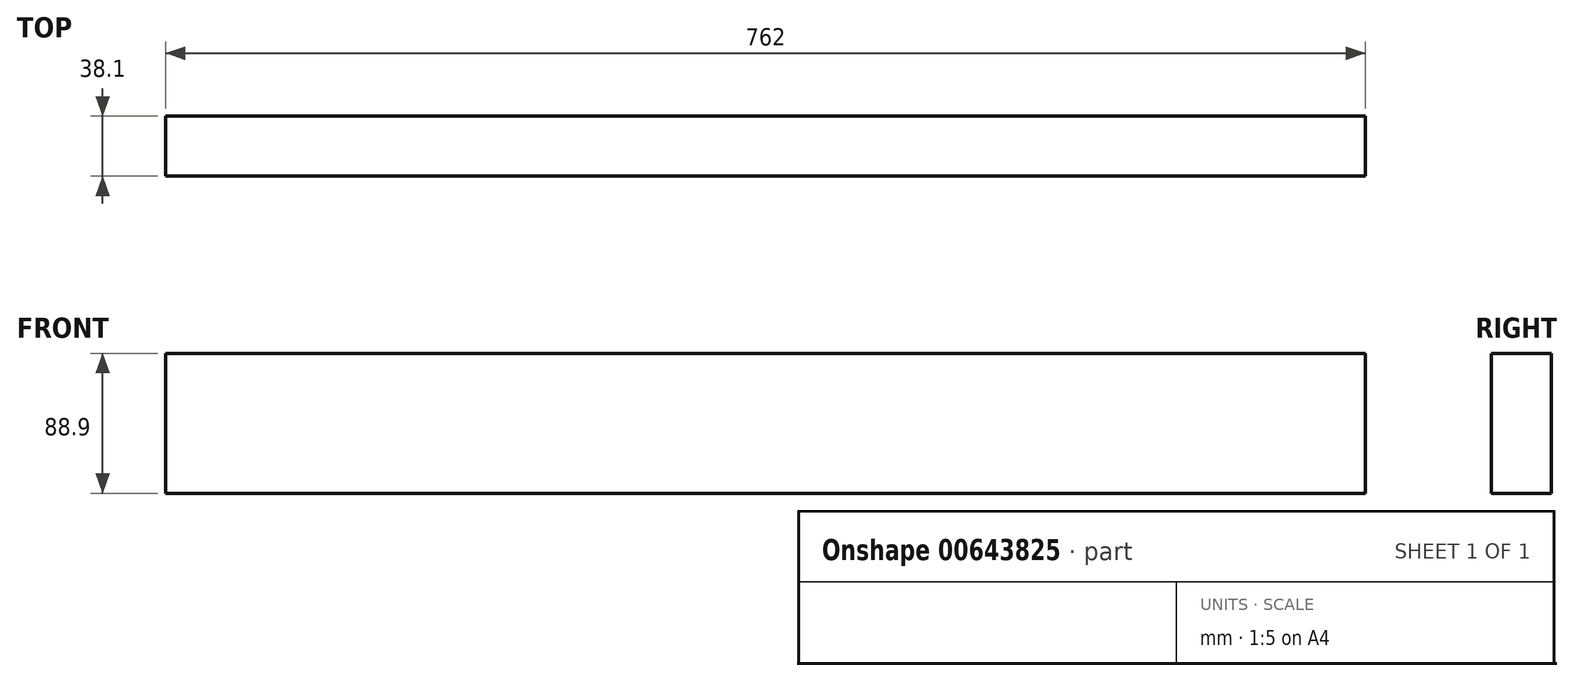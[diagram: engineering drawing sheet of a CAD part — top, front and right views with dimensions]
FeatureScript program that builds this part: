
annotation { "Feature Type Name" : "Feature", "Feature Type Description" : "" }
export const myFeature = defineFeature(function(context is Context, id is Id, definition is map)
    precondition{}
    {
        {
            var Q0;
            Q0=qCreatedBy(makeId("Front.planeOp"),FACE);
            var sketch = newSketch(context, id + "F0", { "sketchPlane" : qUnion([Q0])});
            skLineSegment(sketch, "E0.bottom", {"start": v(-378.14, 35.25) * mm, "end": v(383.86, 35.25) * mm});
            skLineSegment(sketch, "E0.top", {"start": v(-378.14, -53.65) * mm, "end": v(383.86, -53.65) * mm});
            skLineSegment(sketch, "E0.left", {"start": v(-378.14, 35.25) * mm, "end": v(-378.14, -53.65) * mm});
            skLineSegment(sketch, "E0.right", {"start": v(383.86, 35.25) * mm, "end": v(383.86, -53.65) * mm});
            skSolve(sketch);
        }
        {
            var Q0;
            Q0=makeQuery(id+"F0.imprint","IMPRINT",FACE,{"disambiguationData":[TD([[makeQuery(id+"F0.imprint","IMPRINT",EDGE,{"derivedFrom":sQuery(id+"F0.wireOp",EDGE,"E0.bottom")}),-1.0]])]});
            extrude(context, id + "F1", {"entities" : qUnion([Q0]), "depth" : 38.1 * mm, "offsetDistance" : 25.4 * mm});
        }
    });
